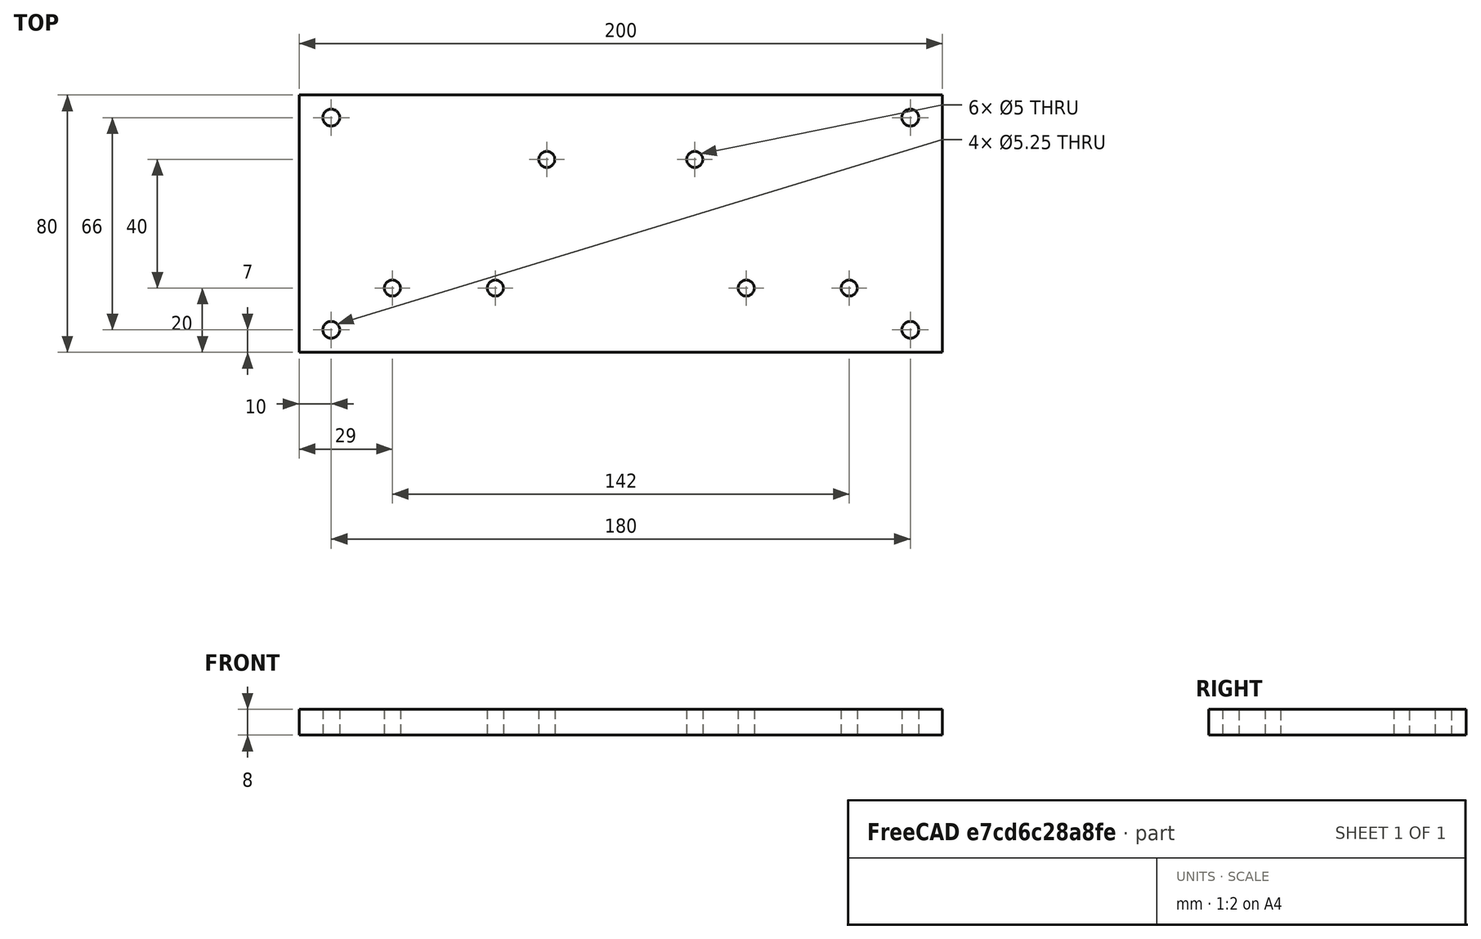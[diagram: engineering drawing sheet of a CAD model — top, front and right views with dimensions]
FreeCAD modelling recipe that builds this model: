
FCSTD DOCUMENT  (FreeCAD 0.15R4671 (Git))
Label: base-left
License: All rights reserved
LicenseURL: http://en.wikipedia.org/wiki/All_rights_reserved
objects: Drawing::FeatureView×21, Drawing::FeatureViewPart×2, Sketcher::SketchObject×1, PartDesign::Pad×1, Drawing::FeaturePage×1
note: 3 computed .brp shape members not serialized (recipe doc carries the construction recipe); baked Part::Feature solids carry a one-line shape summary decoded from their .brp

FEATURE [Sketcher::SketchObject] Sketch  label="main-sketch"
  Placement = pos=(0,0,0) rot=(0,0,1;1.5708rad)
  sketch-geometry (24):
    g0: LineSegment StartX=-40 StartY=100 StartZ=0 EndX=40 EndY=100 EndZ=0
    g1: LineSegment StartX=40 StartY=100 StartZ=0 EndX=40 EndY=-100 EndZ=0
    g2: LineSegment StartX=40 StartY=-100 StartZ=0 EndX=-40 EndY=-100 EndZ=0
    g3: LineSegment StartX=-40 StartY=-100 StartZ=0 EndX=-40 EndY=100 EndZ=0
    g4: LineSegment [constr] StartX=-33 StartY=90 StartZ=0 EndX=33 EndY=90 EndZ=0
    g5: LineSegment [constr] StartX=33 StartY=90 StartZ=0 EndX=33 EndY=-90 EndZ=0
    g6: LineSegment [constr] StartX=33 StartY=-90 StartZ=0 EndX=-33 EndY=-90 EndZ=0
    g7: LineSegment [constr] StartX=-33 StartY=-90 StartZ=0 EndX=-33 EndY=90 EndZ=0
    g8: GeomPoint [constr] X=20 Y=0 Z=0
    g9: LineSegment [constr] StartX=20 StartY=90 StartZ=0 EndX=20 EndY=-90 EndZ=0
    g10: Circle CenterX=20 CenterY=23 CenterZ=0 NormalX=0 NormalY=0 NormalZ=1 Radius=2.5
    g11: Circle CenterX=20 CenterY=-23 CenterZ=0 NormalX=0 NormalY=0 NormalZ=1 Radius=2.5
    g12: GeomPoint [constr] X=20 Y=30 Z=0
    g13: GeomPoint [constr] X=20 Y=34 Z=0
    g14: LineSegment [constr] StartX=20 StartY=39 StartZ=0 EndX=-33 EndY=39 EndZ=0
    g15: LineSegment [constr] StartX=-20 StartY=90 StartZ=0 EndX=-20 EndY=-90 EndZ=0
    g16: Circle CenterX=-20 CenterY=39 CenterZ=0 NormalX=0 NormalY=0 NormalZ=1 Radius=2.5
    g17: Circle CenterX=-20 CenterY=-39 CenterZ=0 NormalX=0 NormalY=0 NormalZ=1 Radius=2.5
    g18: Circle CenterX=-20 CenterY=71 CenterZ=0 NormalX=0 NormalY=0 NormalZ=1 Radius=2.5
    g19: Circle CenterX=-20 CenterY=-71 CenterZ=0 NormalX=0 NormalY=0 NormalZ=1 Radius=2.5
    g20: Circle CenterX=-33 CenterY=90 CenterZ=0 NormalX=0 NormalY=0 NormalZ=1 Radius=2.625
    g21: Circle CenterX=33 CenterY=90 CenterZ=0 NormalX=0 NormalY=0 NormalZ=1 Radius=2.625
    g22: Circle CenterX=-33 CenterY=-90 CenterZ=0 NormalX=0 NormalY=0 NormalZ=1 Radius=2.625
    g23: Circle CenterX=33 CenterY=-90 CenterZ=0 NormalX=0 NormalY=0 NormalZ=1 Radius=2.625
  constraints (66):
    c: Coincident(g0,g1)
    c: Coincident(g1,g2)
    c: Horizontal(g2)
    c: Vertical(g1)
    c: Coincident(g4,g5)
    c: Coincident(g5,g6)
    c: Coincident(g6,g7)
    c: Coincident(g7,g4)
    c: Horizontal(g4)
    c: Horizontal(g6)
    c: Vertical(g5)
    c: Vertical(g7)
    c: Symmetric(g4,g4,g-2)
    c: Symmetric(g0,g0,g-2)
    c: Symmetric(g0,g2,g-1)
    c: Symmetric(g4,g5,g-1)
    c: DistanceY(g0,g4) = -10
    c: DistanceX(g4,g0) = -7
    c: Coincident(g3,g2)
    c: Coincident(g3,g0)
    c: PointOnObject(g8,g-1)
    c: Distance(g8,g1) = 20
    c: PointOnObject(g9,g4)
    c: PointOnObject(g9,g6)
    c: Vertical(g9)
    c: PointOnObject(g8,g9)
    c: PointOnObject(g10,g9)
    c: PointOnObject(g11,g9)
    c: DistanceY(g0,g1) = -200
    c: Symmetric(g10,g11,g-1)
    c: DistanceY(g10,g11) = -46
    c: PointOnObject(g12,g9)
    c: DistanceY(g12,g10) = -7
    c: PointOnObject(g13,g9)
    c: DistanceY(g13,g12) = -4
    c: PointOnObject(g14,g9)
    c: PointOnObject(g14,g7)
    c: Horizontal(g14)
    c: DistanceY(g14,g13) = -5
    c: PointOnObject(g15,g4)
    c: PointOnObject(g15,g6)
    c: Vertical(g15)
    c: DistanceX(g15,g9) = 40
    c: PointOnObject(g16,g14)
    c: PointOnObject(g16,g15)
    c: Radius(g10) = 2.5
    c: Equal(g10,g11)
    c: PointOnObject(g17,g15)
    c: Symmetric(g17,g16,g-1)
    c: PointOnObject(g18,g15)
    c: PointOnObject(g19,g15)
    c: DistanceY(g17,g19) = -32
    c: DistanceY(g16,g18) = 32
    c: Radius(g18) = 2.5
    c: Equal(g18,g16)
    c: Equal(g18,g17)
    c: Equal(g18,g19)
    c: Coincident(g20,g4)
    c: Coincident(g21,g4)
    c: Coincident(g22,g6)
    c: Coincident(g23,g5)
    c: Radius(g22) = 2.625
    c: Equal(g22,g23)
    c: Equal(g22,g21)
    c: Equal(g22,g20)
    c: DistanceX(g15,g0) = -20
FEATURE [PartDesign::Pad] Pad  label="base-left"
  Length = 8
  Length2 = 100
  Placement = pos=(0,0,0) rot=(0,0,1;1.5708rad)
  Sketch = -> Sketch
  Type = 0
FEATURE [Drawing::FeatureViewPart] Ortho  label="Ortho_0_0"
  Direction = (0,0,1)
  HiddenWidth = 0.15
  LineWidth = 0.35
  Rotation = 0
  ShowHiddenLines = false
  ShowSmoothLines = false
  Source = -> Pad
  Tolerance = 0.05
  ViewResult = <g id="Ortho_0_0"\n   transform="rotate(0,148.5,81.3333) translate(148.5,81.3333) scale(1,1)"\n  >\n<g   stroke="rgb(0, 0, 0)"\n   stroke-width="0.35"\n   stroke-linecap="butt"\n   stroke-linejoin="miter"\n   fill="none"\n   transform="scale(1,-1)"\n  >\n<path id= "1" d=" M -100 -40 L -100 40 " />\n<path id= "2" d=" M -100 40 L 100 40 " />\n<path id= "3" d=" M 100 40 L 100 -40 " />\n<path id= "4" d=" M 100 -40 L -100 -40 " />\n<circle cx ="90" cy ="33" r ="2.625" /><circle cx ="90" cy ="-33" r ="2.625" /><circle cx ="-90" cy ="33" r ="2.625" /><circle cx ="-90" cy ="-33" r ="2.625" /><circle cx ="71" cy ="-20" r ="2.5" /><circle cx ="-71" cy ="-20" r ="2.5" /><circle cx ="39" cy ="-20" r ="2.5" /><circle cx ="-39" cy ="-20" r ="2.5" /><circle cx ="23" cy ="20" r ="2.5" /><circle cx ="-23" cy ="20" r ="2.5" /></g>\n</g>
  Visible = true
  X = 148.5
  Y = 81.3333
FEATURE [Drawing::FeatureViewPart] Ortho001  label="Ortho_0_-1"
  Direction = (0,-1,0)
  HiddenWidth = 0.15
  LineWidth = 0.35
  Rotation = 90
  ShowHiddenLines = false
  ShowSmoothLines = false
  Source = -> Pad
  Tolerance = 0.05
  ViewResult = <g id="Ortho_0_-1"\n   transform="rotate(90,148.5,168.667) translate(148.5,168.667) scale(1,1)"\n  >\n<g   stroke="rgb(0, 0, 0)"\n   stroke-width="0.35"\n   stroke-linecap="butt"\n   stroke-linejoin="miter"\n   fill="none"\n   transform="scale(1,-1)"\n  >\n<path id= "1" d=" M 0 -100 L -8 -100 " />\n<path id= "2" d=" M 0 100 L -8 100 " />\n<path id= "3" d=" M 0 100 L 0 -100 " />\n<path id= "4" d=" M -8 100 L -8 -100 " />\n</g>\n</g>
  Visible = true
  X = 148.5
  Y = 168.667
FEATURE [Drawing::FeatureView] dim001
  Rotation = 0
  ViewResult = <g> \n  <line x1="46.500000" y1="41.333300" x2="19.393485" y2="41.333300" style="stroke:rgb(0,0,255);stroke-width:0.50" />\n<line x1="46.500000" y1="121.333300" x2="19.393485" y2="121.333300" style="stroke:rgb(0,0,255);stroke-width:0.50" />\n<line x1="20.393485" y1="41.333300" x2="20.393485" y2="121.333300" style="stroke:rgb(0,0,255);stroke-width:0.50" /> \n  <polygon points="20.393485,121.333300 21.393485,118.333300 20.393485,117.333300 19.393485,118.333300" style="fill:rgb(0,0,255);stroke:rgb(0,0,255);stroke-width:0" /><polygon points="20.393485,41.333300 19.393485,44.333300 20.393485,45.333300 21.393485,44.333300" style="fill:rgb(0,0,255);stroke:rgb(0,0,255);stroke-width:0" /> \n  <text x="18.393485" y="81.333300" font-family="inherit" font-size="3.6" fill="rgb(0,0,255)" text-anchor="middle" transform="rotate(-90.000000 18.393485,81.333300)" >80</text> </g>
  Visible = true
  X = 0
  Y = 0
FEATURE [Drawing::FeatureView] dim002
  Rotation = 0
  ViewResult = <g> \n  <line x1="56.500000" y1="48.333300" x2="28.957778" y2="48.333300" style="stroke:rgb(0,0,255);stroke-width:0.50" />\n<line x1="56.500000" y1="114.333300" x2="28.957778" y2="114.333300" style="stroke:rgb(0,0,255);stroke-width:0.50" />\n<line x1="29.957778" y1="48.333300" x2="29.957778" y2="114.333300" style="stroke:rgb(0,0,255);stroke-width:0.50" /> \n  <polygon points="29.957778,114.333300 30.957778,111.333300 29.957778,110.333300 28.957778,111.333300" style="fill:rgb(0,0,255);stroke:rgb(0,0,255);stroke-width:0" /><polygon points="29.957778,48.333300 28.957778,51.333300 29.957778,52.333300 30.957778,51.333300" style="fill:rgb(0,0,255);stroke:rgb(0,0,255);stroke-width:0" /> \n  <text x="27.957778" y="81.333300" font-family="inherit" font-size="3.6" fill="rgb(0,0,255)" text-anchor="middle" transform="rotate(-90.000000 27.957778,81.333300)" >66</text> </g>
  Visible = true
  X = 0
  Y = 0
FEATURE [Drawing::FeatureView] dim003
  Rotation = 0
  ViewResult = <g> \n  <line x1="48.500000" y1="39.333300" x2="48.500000" y2="13.443929" style="stroke:rgb(0,0,255);stroke-width:0.50" />\n<line x1="248.500000" y1="39.333300" x2="248.500000" y2="13.443929" style="stroke:rgb(0,0,255);stroke-width:0.50" />\n<line x1="48.500000" y1="14.443929" x2="248.500000" y2="14.443929" style="stroke:rgb(0,0,255);stroke-width:0.50" /> \n  <polygon points="248.500000,14.443929 245.500000,13.443929 244.500000,14.443929 245.500000,15.443929" style="fill:rgb(0,0,255);stroke:rgb(0,0,255);stroke-width:0" /><polygon points="48.500000,14.443929 51.500000,15.443929 52.500000,14.443929 51.500000,13.443929" style="fill:rgb(0,0,255);stroke:rgb(0,0,255);stroke-width:0" /> \n  <text x="148.500000" y="12.443929" font-family="inherit" font-size="3.6" fill="rgb(0,0,255)" text-anchor="middle" transform="rotate(0.000000 148.500000,12.443929)" >200</text> </g>
  Visible = true
  X = 0
  Y = 0
FEATURE [Drawing::FeatureView] centerLines001
  Rotation = 0
  ViewResult = <g transform="scale(1.000000,1.000000)" stroke="rgb(0,0,255)"  stroke-width="0.320000" > <path d="M 148.500000,41.333300 L 148.500000,44.333300 M 148.500000,46.333300 L 148.500000,52.333300 M 148.500000,54.333300 L 148.500000,57.333300 M 148.500000,59.333300 L 148.500000,65.333300 M 148.500000,67.333300 L 148.500000,70.333300 M 148.500000,72.333300 L 148.500000,78.333300 M 148.500000,80.333300 L 148.500000,83.333300 M 148.500000,85.333300 L 148.500000,91.333300 M 148.500000,93.333300 L 148.500000,96.333300 M 148.500000,98.333300 L 148.500000,104.333300 M 148.500000,106.333300 L 148.500000,109.333300 M 148.500000,111.333300 L 148.500000,117.333300 M 148.500000,119.333300 L 148.500000,122.333300 "/>\n<path d="M 148.500000,41.333300 L 148.500000,44.333300 M 148.500000,46.333300 L 148.500000,52.333300 M 148.500000,54.333300 L 148.500000,57.333300 M 148.500000,59.333300 L 148.500000,65.333300 M 148.500000,67.333300 L 148.500000,70.333300 M 148.500000,72.333300 L 148.500000,78.333300 M 148.500000,80.333300 L 148.500000,83.333300 M 148.500000,85.333300 L 148.500000,91.333300 M 148.500000,93.333300 L 148.500000,96.333300 M 148.500000,98.333300 L 148.500000,104.333300 M 148.500000,106.333300 L 148.500000,109.333300 M 148.500000,111.333300 L 148.500000,117.333300 M 148.500000,119.333300 L 148.500000,122.333300 "/> </g> 
  Visible = true
  X = 0
  Y = 0
FEATURE [Drawing::FeatureView] centerLines002
  Rotation = 0
  ViewResult = <blob: 2986 chars omitted>
  Visible = true
  X = 0
  Y = 0
FEATURE [Drawing::FeatureView] dim004
  Rotation = 0
  ViewResult = <g> \n  <line x1="58.500000" y1="46.333300" x2="58.500000" y2="22.206379" style="stroke:rgb(0,0,255);stroke-width:0.50" />\n<line x1="238.500000" y1="46.333300" x2="238.500000" y2="22.206379" style="stroke:rgb(0,0,255);stroke-width:0.50" />\n<line x1="58.500000" y1="23.206379" x2="238.500000" y2="23.206379" style="stroke:rgb(0,0,255);stroke-width:0.50" /> \n  <polygon points="238.500000,23.206379 235.500000,22.206379 234.500000,23.206379 235.500000,24.206379" style="fill:rgb(0,0,255);stroke:rgb(0,0,255);stroke-width:0" /><polygon points="58.500000,23.206379 61.500000,24.206379 62.500000,23.206379 61.500000,22.206379" style="fill:rgb(0,0,255);stroke:rgb(0,0,255);stroke-width:0" /> \n  <text x="148.500000" y="21.206379" font-family="inherit" font-size="3.6" fill="rgb(0,0,255)" text-anchor="middle" transform="rotate(0.000000 148.500000,21.206379)" >180</text> </g>
  Visible = true
  X = 0
  Y = 0
FEATURE [Drawing::FeatureView] dim006
  Rotation = 0
  ViewResult = <g> \n  <line x1="77.500000" y1="103.333300" x2="77.500000" y2="147.686121" style="stroke:rgb(0,0,255);stroke-width:0.50" />\n<line x1="219.500000" y1="103.333300" x2="219.500000" y2="147.686121" style="stroke:rgb(0,0,255);stroke-width:0.50" />\n<line x1="77.500000" y1="146.686121" x2="219.500000" y2="146.686121" style="stroke:rgb(0,0,255);stroke-width:0.50" /> \n  <polygon points="219.500000,146.686121 216.500000,145.686121 215.500000,146.686121 216.500000,147.686121" style="fill:rgb(0,0,255);stroke:rgb(0,0,255);stroke-width:0" /><polygon points="77.500000,146.686121 80.500000,147.686121 81.500000,146.686121 80.500000,145.686121" style="fill:rgb(0,0,255);stroke:rgb(0,0,255);stroke-width:0" /> \n  <text x="148.500000" y="144.686121" font-family="inherit" font-size="3.6" fill="rgb(0,0,255)" text-anchor="middle" transform="rotate(0.000000 148.500000,144.686121)" >142</text> </g>
  Visible = true
  X = 0
  Y = 0
FEATURE [Drawing::FeatureView] dim007
  Rotation = 0
  ViewResult = <g> \n  <line x1="77.500000" y1="103.333300" x2="77.500000" y2="139.478801" style="stroke:rgb(0,0,255);stroke-width:0.50" />\n<line x1="109.500000" y1="103.333300" x2="109.500000" y2="139.478801" style="stroke:rgb(0,0,255);stroke-width:0.50" />\n<line x1="77.500000" y1="138.478801" x2="109.500000" y2="138.478801" style="stroke:rgb(0,0,255);stroke-width:0.50" /> \n  <polygon points="109.500000,138.478801 106.500000,137.478801 105.500000,138.478801 106.500000,139.478801" style="fill:rgb(0,0,255);stroke:rgb(0,0,255);stroke-width:0" /><polygon points="77.500000,138.478801 80.500000,139.478801 81.500000,138.478801 80.500000,137.478801" style="fill:rgb(0,0,255);stroke:rgb(0,0,255);stroke-width:0" /> \n  <text x="93.500000" y="136.478801" font-family="inherit" font-size="3.6" fill="rgb(0,0,255)" text-anchor="middle" transform="rotate(0.000000 93.500000,136.478801)" >32</text> </g>
  Visible = true
  X = 0
  Y = 0
FEATURE [Drawing::FeatureView] dim008
  Rotation = 0
  ViewResult = <g> \n  <line x1="187.500000" y1="103.333300" x2="187.500000" y2="137.860683" style="stroke:rgb(0,0,255);stroke-width:0.50" />\n<line x1="219.500000" y1="103.333300" x2="219.500000" y2="137.860683" style="stroke:rgb(0,0,255);stroke-width:0.50" />\n<line x1="187.500000" y1="136.860683" x2="219.500000" y2="136.860683" style="stroke:rgb(0,0,255);stroke-width:0.50" /> \n  <polygon points="219.500000,136.860683 216.500000,135.860683 215.500000,136.860683 216.500000,137.860683" style="fill:rgb(0,0,255);stroke:rgb(0,0,255);stroke-width:0" /><polygon points="187.500000,136.860683 190.500000,137.860683 191.500000,136.860683 190.500000,135.860683" style="fill:rgb(0,0,255);stroke:rgb(0,0,255);stroke-width:0" /> \n  <text x="203.500000" y="134.860683" font-family="inherit" font-size="3.6" fill="rgb(0,0,255)" text-anchor="middle" transform="rotate(0.000000 203.500000,134.860683)" >32</text> </g>
  Visible = true
  X = 0
  Y = 0
FEATURE [Drawing::FeatureView] dim011
  Rotation = 0
  ViewResult = <g>  <circle cx ="77.500000" cy ="101.333300" r="0.250000" stroke="none" fill="rgb(0,0,255)" /> \n<line x1="81.271173" y1="96.678030" x2="75.926344" y2="103.275877" style="stroke:rgb(0,0,255);stroke-width:0.50" />\n<polygon points="79.073656,99.390723 81.739074,97.689093 81.591506,96.282599 80.185013,96.430168" style="fill:rgb(0,0,255);stroke:rgb(0,0,255);stroke-width:0" />\n<polygon points="75.926344,103.275877 73.260926,104.977507 73.408494,106.384001 74.814987,106.236432" style="fill:rgb(0,0,255);stroke:rgb(0,0,255);stroke-width:0" />\n<line x1="81.271173" y1="96.678030" x2="93.211487" y2="96.678030" style="stroke:rgb(0,0,255);stroke-width:0.50" />\n<text x="87.241330" y="94.678030" font-family="inherit" font-size="3.6" fill="rgb(0,0,255)" text-anchor="middle"  >2 x Ø5</text> </g>
  Visible = true
  X = 0
  Y = 0
FEATURE [Drawing::FeatureView] dim012
  Rotation = 0
  ViewResult = <g>  <circle cx ="187.500000" cy ="101.333300" r="0.250000" stroke="none" fill="rgb(0,0,255)" /> \n<line x1="190.659860" y1="97.063202" x2="186.012896" y2="103.342908" style="stroke:rgb(0,0,255);stroke-width:0.50" />\n<polygon points="188.987104,99.323692 191.575471,97.507005 191.366470,96.108320 189.967785,96.317322" style="fill:rgb(0,0,255);stroke:rgb(0,0,255);stroke-width:0" />\n<polygon points="186.012896,103.342908 183.424529,105.159595 183.633530,106.558280 185.032215,106.349278" style="fill:rgb(0,0,255);stroke:rgb(0,0,255);stroke-width:0" />\n<line x1="190.659860" y1="97.063202" x2="204.140860" y2="97.063202" style="stroke:rgb(0,0,255);stroke-width:0.50" />\n<text x="197.400360" y="95.063202" font-family="inherit" font-size="3.6" fill="rgb(0,0,255)" text-anchor="middle"  >2 x Ø5</text> </g>
  Visible = true
  X = 0
  Y = 0
FEATURE [Drawing::FeatureView] dim013
  Rotation = 0
  ViewResult = <g>  <circle cx ="125.500000" cy ="61.333300" r="0.250000" stroke="none" fill="rgb(0,0,255)" /> \n<line x1="129.417602" y1="56.620201" x2="123.901943" y2="63.255854" style="stroke:rgb(0,0,255);stroke-width:0.50" />\n<polygon points="127.098057,59.410746 129.784747,57.742904 129.654948,56.334660 128.246704,56.464459" style="fill:rgb(0,0,255);stroke:rgb(0,0,255);stroke-width:0" />\n<polygon points="123.901943,63.255854 121.215253,64.923696 121.345052,66.331940 122.753296,66.202141" style="fill:rgb(0,0,255);stroke:rgb(0,0,255);stroke-width:0" />\n<line x1="129.417602" y1="56.620201" x2="139.432059" y2="56.620201" style="stroke:rgb(0,0,255);stroke-width:0.50" />\n<text x="134.424831" y="54.620201" font-family="inherit" font-size="3.6" fill="rgb(0,0,255)" text-anchor="middle"  >2 x Ø5</text> </g>
  Visible = true
  X = 0
  Y = 0
FEATURE [Drawing::FeatureView] dim010
  Rotation = 0
  ViewResult = <g>  <circle cx ="58.500000" cy ="48.333300" r="0.250000" stroke="none" fill="rgb(0,0,255)" /> \n<line x1="65.518689" y1="37.212071" x2="57.099017" y2="50.553181" style="stroke:rgb(0,0,255);stroke-width:0.50" />\n<polygon points="59.900983,46.113419 62.347776,44.110120 62.035815,42.730743 60.656438,43.042704" style="fill:rgb(0,0,255);stroke:rgb(0,0,255);stroke-width:0" />\n<polygon points="57.099017,50.553181 54.652224,52.556480 54.964185,53.935857 56.343562,53.623896" style="fill:rgb(0,0,255);stroke:rgb(0,0,255);stroke-width:0" />\n<line x1="65.518689" y1="37.212071" x2="77.922713" y2="37.212071" style="stroke:rgb(0,0,255);stroke-width:0.50" />\n<text x="71.720701" y="35.212071" font-family="inherit" font-size="3.6" fill="rgb(0,0,255)" text-anchor="middle"  >4 x Ø5.25</text> </g>
  Visible = true
  X = 0
  Y = 0
FEATURE [Drawing::FeatureView] dim014
  Rotation = 0
  ViewResult = <g> \n  <line x1="173.500000" y1="61.333300" x2="274.934720" y2="61.333300" style="stroke:rgb(0,0,255);stroke-width:0.50" />\n<line x1="250.500000" y1="41.333300" x2="274.934720" y2="41.333300" style="stroke:rgb(0,0,255);stroke-width:0.50" />\n<line x1="273.934720" y1="61.333300" x2="273.934720" y2="41.333300" style="stroke:rgb(0,0,255);stroke-width:0.50" /> \n  <polygon points="273.934720,41.333300 272.934720,44.333300 273.934720,45.333300 274.934720,44.333300" style="fill:rgb(0,0,255);stroke:rgb(0,0,255);stroke-width:0" /><polygon points="273.934720,61.333300 274.934720,58.333300 273.934720,57.333300 272.934720,58.333300" style="fill:rgb(0,0,255);stroke:rgb(0,0,255);stroke-width:0" /> \n  <text x="271.934720" y="51.333300" font-family="inherit" font-size="3.6" fill="rgb(0,0,255)" text-anchor="middle" transform="rotate(-90.000000 271.934720,51.333300)" >20</text> </g>
  Visible = true
  X = 0
  Y = 0
FEATURE [Drawing::FeatureView] dim015
  Rotation = 0
  ViewResult = <g> \n  <line x1="221.500000" y1="101.333300" x2="275.918425" y2="101.333300" style="stroke:rgb(0,0,255);stroke-width:0.50" />\n<line x1="250.500000" y1="121.333300" x2="275.918425" y2="121.333300" style="stroke:rgb(0,0,255);stroke-width:0.50" />\n<line x1="274.918425" y1="101.333300" x2="274.918425" y2="121.333300" style="stroke:rgb(0,0,255);stroke-width:0.50" /> \n  <polygon points="274.918425,121.333300 275.918425,118.333300 274.918425,117.333300 273.918425,118.333300" style="fill:rgb(0,0,255);stroke:rgb(0,0,255);stroke-width:0" /><polygon points="274.918425,101.333300 273.918425,104.333300 274.918425,105.333300 275.918425,104.333300" style="fill:rgb(0,0,255);stroke:rgb(0,0,255);stroke-width:0" /> \n  <text x="272.918425" y="111.333300" font-family="inherit" font-size="3.6" fill="rgb(0,0,255)" text-anchor="middle" transform="rotate(-90.000000 272.918425,111.333300)" >20</text> </g>
  Visible = true
  X = 0
  Y = 0
FEATURE [Drawing::FeatureView] dim009
  Rotation = 0
  ViewResult = <g> \n  <line x1="46.500000" y1="160.667000" x2="35.931289" y2="160.667000" style="stroke:rgb(0,0,255);stroke-width:0.50" />\n<line x1="46.500000" y1="168.667000" x2="35.931289" y2="168.667000" style="stroke:rgb(0,0,255);stroke-width:0.50" />\n<line x1="36.931289" y1="160.667000" x2="36.931289" y2="168.667000" style="stroke:rgb(0,0,255);stroke-width:0.50" /> \n  <polygon points="36.931289,168.667000 35.931289,171.667000 36.931289,172.667000 37.931289,171.667000" style="fill:rgb(0,0,255);stroke:rgb(0,0,255);stroke-width:0" /><polygon points="36.931289,160.667000 37.931289,157.667000 36.931289,156.667000 35.931289,157.667000" style="fill:rgb(0,0,255);stroke:rgb(0,0,255);stroke-width:0" /> \n  <text x="34.931289" y="164.667000" font-family="inherit" font-size="3.6" fill="rgb(0,0,255)" text-anchor="middle" transform="rotate(-90.000000 34.931289,164.667000)" >8</text> </g>
  Visible = true
  X = 0
  Y = 0
FEATURE [Drawing::FeatureView] dim016
  Rotation = 0
  ViewResult = <g> \n  <line x1="58.500000" y1="46.333300" x2="58.500000" y2="22.234142" style="stroke:rgb(0,0,255);stroke-width:0.50" />\n<line x1="48.500000" y1="39.333300" x2="48.500000" y2="22.234142" style="stroke:rgb(0,0,255);stroke-width:0.50" />\n<line x1="58.500000" y1="23.234142" x2="48.500000" y2="23.234142" style="stroke:rgb(0,0,255);stroke-width:0.50" /> \n  <polygon points="48.500000,23.234142 45.500000,22.234142 44.500000,23.234142 45.500000,24.234142" style="fill:rgb(0,0,255);stroke:rgb(0,0,255);stroke-width:0" /><polygon points="58.500000,23.234142 61.500000,24.234142 62.500000,23.234142 61.500000,22.234142" style="fill:rgb(0,0,255);stroke:rgb(0,0,255);stroke-width:0" /> \n  <text x="53.500000" y="21.234142" font-family="inherit" font-size="3.6" fill="rgb(0,0,255)" text-anchor="middle" transform="rotate(0.000000 53.500000,21.234142)" >10</text> </g>
  Visible = true
  X = 0
  Y = 0
FEATURE [Drawing::FeatureView] dim017
  Rotation = 0
  ViewResult = <g> \n  <line x1="56.500000" y1="114.333300" x2="28.951767" y2="114.333300" style="stroke:rgb(0,0,255);stroke-width:0.50" />\n<line x1="46.500000" y1="121.333300" x2="28.951767" y2="121.333300" style="stroke:rgb(0,0,255);stroke-width:0.50" />\n<line x1="29.951767" y1="114.333300" x2="29.951767" y2="121.333300" style="stroke:rgb(0,0,255);stroke-width:0.50" /> \n  <polygon points="29.951767,121.333300 28.951767,124.333300 29.951767,125.333300 30.951767,124.333300" style="fill:rgb(0,0,255);stroke:rgb(0,0,255);stroke-width:0" /><polygon points="29.951767,114.333300 30.951767,111.333300 29.951767,110.333300 28.951767,111.333300" style="fill:rgb(0,0,255);stroke:rgb(0,0,255);stroke-width:0" /> \n  <text x="27.951767" y="117.833300" font-family="inherit" font-size="3.6" fill="rgb(0,0,255)" text-anchor="middle" transform="rotate(-90.000000 27.951767,117.833300)" >7</text> </g>
  Visible = true
  X = 0
  Y = 0
FEATURE [Drawing::FeatureView] dim018
  Rotation = 0
  ViewResult = <g> \n  <line x1="48.500000" y1="123.333300" x2="48.500000" y2="147.730545" style="stroke:rgb(0,0,255);stroke-width:0.50" />\n<line x1="77.500000" y1="103.333300" x2="77.500000" y2="147.730545" style="stroke:rgb(0,0,255);stroke-width:0.50" />\n<line x1="48.500000" y1="146.730545" x2="77.500000" y2="146.730545" style="stroke:rgb(0,0,255);stroke-width:0.50" /> \n  <polygon points="77.500000,146.730545 74.500000,145.730545 73.500000,146.730545 74.500000,147.730545" style="fill:rgb(0,0,255);stroke:rgb(0,0,255);stroke-width:0" /><polygon points="48.500000,146.730545 51.500000,147.730545 52.500000,146.730545 51.500000,145.730545" style="fill:rgb(0,0,255);stroke:rgb(0,0,255);stroke-width:0" /> \n  <text x="63.000000" y="144.730545" font-family="inherit" font-size="3.6" fill="rgb(0,0,255)" text-anchor="middle" transform="rotate(0.000000 63.000000,144.730545)" >29</text> </g>
  Visible = true
  X = 0
  Y = 0
FEATURE [Drawing::FeatureView] dim019
  Rotation = 0
  ViewResult = <g> \n  <line x1="58.500000" y1="46.333300" x2="58.500000" y2="29.805360" style="stroke:rgb(0,0,255);stroke-width:0.50" />\n<line x1="125.500000" y1="59.333300" x2="125.500000" y2="29.805360" style="stroke:rgb(0,0,255);stroke-width:0.50" />\n<line x1="58.500000" y1="30.805360" x2="125.500000" y2="30.805360" style="stroke:rgb(0,0,255);stroke-width:0.50" /> \n  <polygon points="125.500000,30.805360 122.500000,29.805360 121.500000,30.805360 122.500000,31.805360" style="fill:rgb(0,0,255);stroke:rgb(0,0,255);stroke-width:0" /><polygon points="58.500000,30.805360 61.500000,31.805360 62.500000,30.805360 61.500000,29.805360" style="fill:rgb(0,0,255);stroke:rgb(0,0,255);stroke-width:0" /> \n  <text x="92.000000" y="28.805360" font-family="inherit" font-size="3.6" fill="rgb(0,0,255)" text-anchor="middle" transform="rotate(0.000000 92.000000,28.805360)" >67</text> </g>
  Visible = true
  X = 0
  Y = 0
FEATURE [Drawing::FeatureView] dim005
  Rotation = 0
  ViewResult = <g> \n  <line x1="125.500000" y1="59.333300" x2="125.500000" y2="29.897942" style="stroke:rgb(0,0,255);stroke-width:0.50" />\n<line x1="171.500000" y1="59.333300" x2="171.500000" y2="29.897942" style="stroke:rgb(0,0,255);stroke-width:0.50" />\n<line x1="125.500000" y1="30.897942" x2="171.500000" y2="30.897942" style="stroke:rgb(0,0,255);stroke-width:0.50" /> \n  <polygon points="171.500000,30.897942 168.500000,29.897942 167.500000,30.897942 168.500000,31.897942" style="fill:rgb(0,0,255);stroke:rgb(0,0,255);stroke-width:0" /><polygon points="125.500000,30.897942 128.500000,31.897942 129.500000,30.897942 128.500000,29.897942" style="fill:rgb(0,0,255);stroke:rgb(0,0,255);stroke-width:0" /> \n  <text x="148.500000" y="28.897942" font-family="inherit" font-size="3.6" fill="rgb(0,0,255)" text-anchor="middle" transform="rotate(0.000000 148.500000,28.897942)" >46</text> </g>
  Visible = true
  X = 0
  Y = 0
FEATURE [Drawing::FeaturePage] Page
  Group = -> [Ortho,Ortho001,dim001,dim002,dim003,centerLines001,centerLines002,dim004,dim006,dim007,dim008,dim011,dim012,dim013,dim010,dim014,dim015,dim009,dim016,dim017,dim018,dim019,dim005]
  Template = <path>
note: 1 file-system path scrubbed to <path> (originals preserved in the JSON sidecar)
